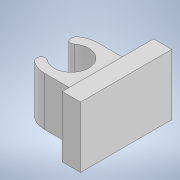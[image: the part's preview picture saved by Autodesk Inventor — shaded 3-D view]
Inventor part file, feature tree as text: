
AUTODESK INVENTOR PART (.ipt)
format: ipt  version: 2020 (Build 240168000, 168)  size: 130,048 bytes
history: native  units: mm
features: extrude x2, fillet x2, other x1, sketch x1
ambient origin geometry x8: Origin, YZ Plane, XZ Plane, XY Plane, X Axis, Y Axis, Z Axis, Center Point
bodies: Body1 (feature_tree)
feature tree (6):
  other  "Твердое тело1"
  sketch  "Эскиз1"
  extrude  "Выдавливание1"  Depth=5.7mm
  extrude  "Выдавливание2"  Depth=13.962634mm
  fillet  "Сопряжение3"  Radius=6.0mm
  fillet  "Сопряжение4"  Radius=8.0mm
